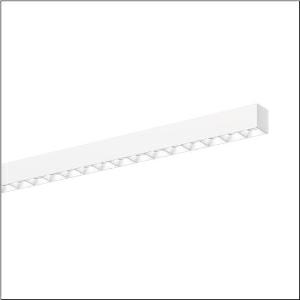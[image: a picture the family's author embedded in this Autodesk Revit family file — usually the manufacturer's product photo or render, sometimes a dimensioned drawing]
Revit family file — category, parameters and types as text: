
# Revit family: silica_r__21_51mx26da34wb_607f
name_source: partatom
category: Lighting Fixtures
units: mm (PartAtom-declared; Revit-internal decimal feet)

## family parameters
Cut with Voids When Loaded = No
Host = Face
Light Source = No
Part Type = Normal
Room Calculation Point = No
Round Connector Dimension = Use Diameter
Shared = No

## types (1)
- --- (1 x LED, 4320 lm, 25.1 W, 3000K)
    Apparent Load = 25 VA
    CIE Flux Codes = 83 98 100 100 100
    Color Rendering = 80
    Color Temperature = 3000K
    Default Elevation = 1800 mm
    Description = Silica® 21, office luminaire, primary light control with darklight reflector, of PMMA, white, CAT 2 (L<= 3000cd/m²), light emission: direct distribution, primary light characteristic: symmetric, installation type: surface-mounted, LED, rated luminous flux: 4.320lm, luminous efficacy: 172lm/W, light colour: 830, colour temperature: 3000K, with terminal, 3+2-pole, max. 2.5mm², mains connection: 220..240V, AC, 50/60Hz, rated input power: 25.1W, luminaire housing, of aluminium, traffic white (RAL 9016), length: 1.204mm, width: 53mm, height: 53mm, protection rating (complete): IP20, insulation class (complete): insulation class I (protective earthing), certification: CE, permissible operating ambient temperature: 0..+35°C, standard: EN 50419, packaging unit: 1 piece
    Height = 0 mm  [stored 0 ft]
    Lamp = 1 x LED
    Lamp Light Flux = 4320 lm
    Lamp Power = 25.1 W
    Lamp count = 1
    Length = 1204 mm
    Luminous efficacy = 172 lm/W
    Manufacturer = Siteco
    ModVariant = No
    Model = 51MX26DA34WB
    Mounting Place = Ceiling
    Mounting Type = Recessed
    Number of Poles = 1
    OnlyDefault = Yes
    Power Factor = 1
    Product Name = Silica® 21
    Product group = office luminaire | ceiling recessed
    ProductGroupID = 401
    Protection Class = Protection class I
    Protection Degree = IP 20
    RLX_Detail_Level = 1
    RLX_Emergency_Light_Flux = 0 lm
    RLX_Emergency_Type = 0
    RLX_Emergency_Type_DB = No
    RlxData = <blob elided: 38169 chars, md5=111a7c58>
    Socket = socket
    Standby Power = 0 W
    System Light Flux = 4320 lm
    System Power = 25 W
    Type Comments = factory setting: luminous flux: 100 % | dim-lin: 254 | 360 mA
    Type Image = l_1297772.jpg
    URL = http://relux.com
    VarID = @adj_055451
    Voltage = 0 V
    Weight = 0.00 kg
    Width = 53 mm

note: [stored X ft] marks values corroborated as IEEE doubles in the binary element streams (Revit-internal decimal feet)

## geometry (parser evidence)
native form markers: Blend x4, Sweep x10
no freeform markers — native parametric forms only
